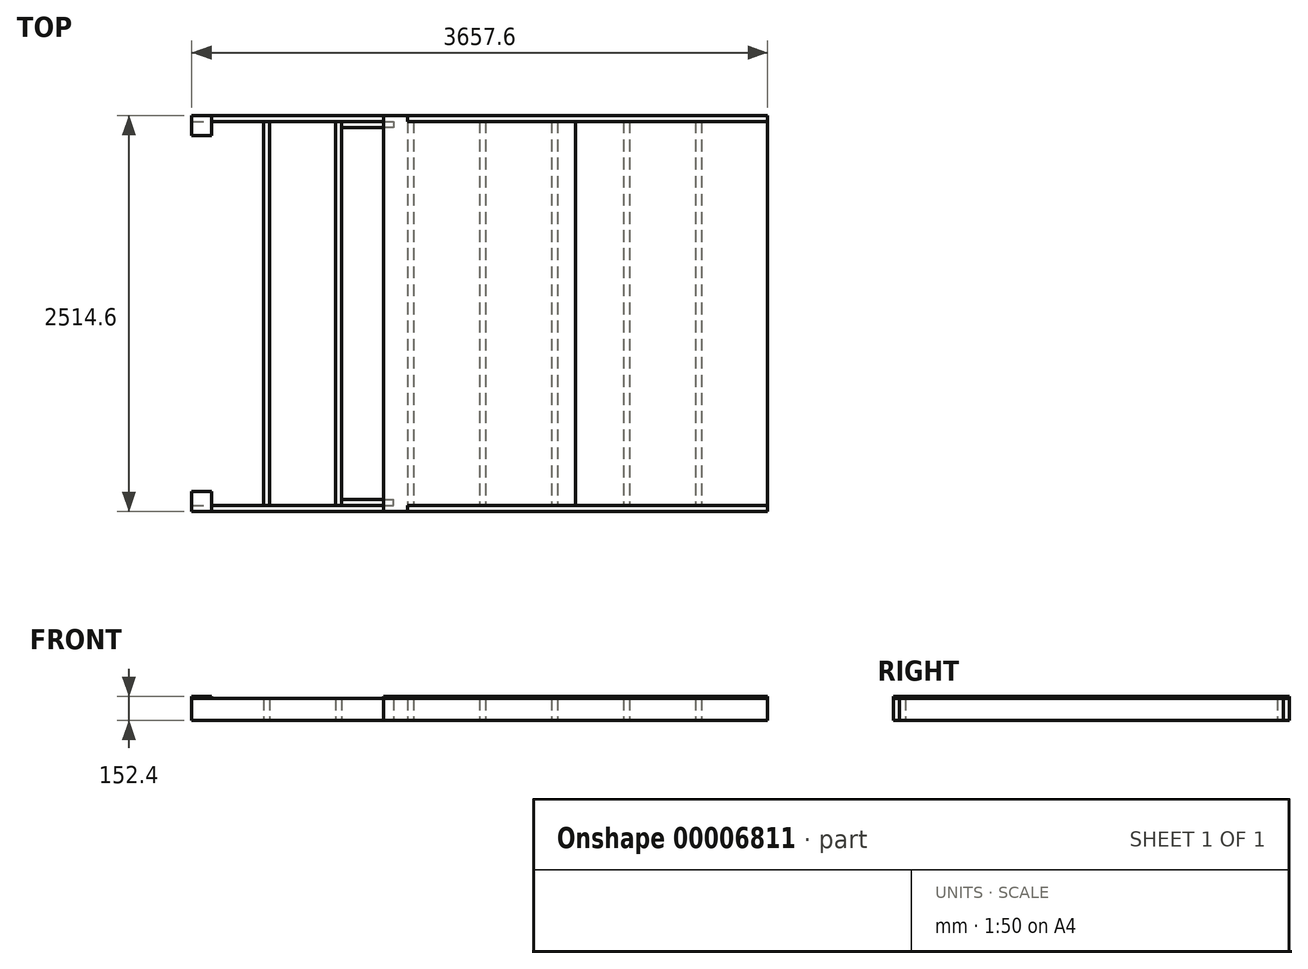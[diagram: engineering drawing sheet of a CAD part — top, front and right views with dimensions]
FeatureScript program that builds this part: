
annotation { "Feature Type Name" : "Feature", "Feature Type Description" : "" }
export const myFeature = defineFeature(function(context is Context, id is Id, definition is map)
    precondition{}
    {
        {
            var Q0;
            Q0=qCreatedBy(makeId("Top.planeOp"),FACE);
            var sketch = newSketch(context, id + "F0", { "sketchPlane" : qUnion([Q0])});
            skLineSegment(sketch, "E0.rect.bottom", {"start": v(1828.8, 1257.3) * mm, "end": v(-1828.8, 1257.3) * mm, "construction": true});
            skLineSegment(sketch, "E0.rect.top", {"start": v(1828.8, -1257.3) * mm, "end": v(-1828.8, -1257.3) * mm, "construction": true});
            skLineSegment(sketch, "E0.rect.left", {"start": v(1828.8, 1257.3) * mm, "end": v(1828.8, -1257.3) * mm, "construction": true});
            skLineSegment(sketch, "E0.rect.right", {"start": v(-1828.8, 1257.3) * mm, "end": v(-1828.8, -1257.3) * mm, "construction": true});
            skPoint(sketch, "E0.rect.middle", {"position": v(0, 0) * mm});
            skLineSegment(sketch, "E1.bottom", {"start": v(-1828.8, 1257.3) * mm, "end": v(-609.6, 1257.3) * mm});
            skLineSegment(sketch, "E1.top", {"start": v(-1828.8, 1219.2) * mm, "end": v(-609.6, 1219.2) * mm});
            skLineSegment(sketch, "E1.left", {"start": v(-1828.8, 1257.3) * mm, "end": v(-1828.8, 1219.2) * mm});
            skLineSegment(sketch, "E1.right", {"start": v(-609.6, 1257.3) * mm, "end": v(-609.6, 1219.2) * mm});
            skLineSegment(sketch, "E2.bottom", {"start": v(-1828.8, -1257.3) * mm, "end": v(-609.6, -1257.3) * mm});
            skLineSegment(sketch, "E2.top", {"start": v(-1828.8, -1219.2) * mm, "end": v(-609.6, -1219.2) * mm});
            skLineSegment(sketch, "E2.left", {"start": v(-1828.8, -1257.3) * mm, "end": v(-1828.8, -1219.2) * mm});
            skLineSegment(sketch, "E2.right", {"start": v(-609.6, -1257.3) * mm, "end": v(-609.6, -1219.2) * mm});
            skLineSegment(sketch, "E3.bottom", {"start": v(-1828.8, 1219.2) * mm, "end": v(-1790.7, 1219.2) * mm});
            skLineSegment(sketch, "E3.top", {"start": v(-1828.8, -1219.2) * mm, "end": v(-1790.7, -1219.2) * mm});
            skLineSegment(sketch, "E3.left", {"start": v(-1828.8, 1219.2) * mm, "end": v(-1828.8, -1219.2) * mm});
            skLineSegment(sketch, "E3.right", {"start": v(-1790.7, 1219.2) * mm, "end": v(-1790.7, -1219.2) * mm});
            skLineSegment(sketch, "E4.1.0.0", {"start": v(-1371.6, 1219.2) * mm, "end": v(-1371.6, -1219.2) * mm});
            skLineSegment(sketch, "E4.1.0.1", {"start": v(-1333.5, 1219.2) * mm, "end": v(-1333.5, -1219.2) * mm});
            skLineSegment(sketch, "E4.2.0.0", {"start": v(-914.4, 1219.2) * mm, "end": v(-914.4, -1219.2) * mm});
            skLineSegment(sketch, "E4.2.0.1", {"start": v(-876.3, 1219.2) * mm, "end": v(-876.3, -1219.2) * mm});
            skLineSegment(sketch, "E4.3.0.0", {"start": v(-457.2, 1219.2) * mm, "end": v(-457.2, -1219.2) * mm});
            skLineSegment(sketch, "E4.3.0.1", {"start": v(-419.1, 1219.2) * mm, "end": v(-419.1, -1219.2) * mm});
            skLineSegment(sketch, "E4.4.0.0", {"start": v(0, 1219.2) * mm, "end": v(0, -1219.2) * mm});
            skLineSegment(sketch, "E4.4.0.1", {"start": v(38.1, 1219.2) * mm, "end": v(38.1, -1219.2) * mm});
            skLineSegment(sketch, "E4.5.0.0", {"start": v(457.2, 1219.2) * mm, "end": v(457.2, -1219.2) * mm});
            skLineSegment(sketch, "E4.5.0.1", {"start": v(495.3, 1219.2) * mm, "end": v(495.3, -1219.2) * mm});
            skLineSegment(sketch, "E4.6.0.0", {"start": v(914.4, 1219.2) * mm, "end": v(914.4, -1219.2) * mm});
            skLineSegment(sketch, "E4.6.0.1", {"start": v(952.5, 1219.2) * mm, "end": v(952.5, -1219.2) * mm});
            skLineSegment(sketch, "E4.7.0.0", {"start": v(1371.6, 1219.2) * mm, "end": v(1371.6, -1219.2) * mm});
            skLineSegment(sketch, "E4.7.0.1", {"start": v(1409.7, 1219.2) * mm, "end": v(1409.7, -1219.2) * mm});
            skLineSegment(sketch, "E4.direction1", {"start": v(-1828.8, -1219.2) * mm, "end": v(-1371.6, -1219.2) * mm, "construction": true});
            skLineSegment(sketch, "E5.bottom", {"start": v(-609.6, -1219.2) * mm, "end": v(1828.8, -1219.2) * mm});
            skLineSegment(sketch, "E5.top", {"start": v(-609.6, -1257.3) * mm, "end": v(1828.8, -1257.3) * mm});
            skLineSegment(sketch, "E5.left", {"start": v(-609.6, -1219.2) * mm, "end": v(-609.6, -1257.3) * mm});
            skLineSegment(sketch, "E5.right", {"start": v(1828.8, -1219.2) * mm, "end": v(1828.8, -1257.3) * mm});
            skLineSegment(sketch, "E6.bottom", {"start": v(-609.6, 1219.2) * mm, "end": v(1828.8, 1219.2) * mm});
            skLineSegment(sketch, "E6.top", {"start": v(-609.6, 1257.3) * mm, "end": v(1828.8, 1257.3) * mm});
            skLineSegment(sketch, "E6.left", {"start": v(-609.6, 1219.2) * mm, "end": v(-609.6, 1257.3) * mm});
            skLineSegment(sketch, "E6.right", {"start": v(1828.8, 1219.2) * mm, "end": v(1828.8, 1257.3) * mm});
            skLineSegment(sketch, "E7.bottom", {"start": v(-546.1, 1219.2) * mm, "end": v(-876.3, 1219.2) * mm});
            skLineSegment(sketch, "E7.top", {"start": v(-546.1, 1181.1) * mm, "end": v(-876.3, 1181.1) * mm});
            skLineSegment(sketch, "E7.left", {"start": v(-546.1, 1219.2) * mm, "end": v(-546.1, 1181.1) * mm});
            skLineSegment(sketch, "E7.right", {"start": v(-876.3, 1219.2) * mm, "end": v(-876.3, 1181.1) * mm});
            skLineSegment(sketch, "E8.bottom", {"start": v(-876.3, -1219.2) * mm, "end": v(-546.1, -1219.2) * mm});
            skLineSegment(sketch, "E8.top", {"start": v(-876.3, -1181.1) * mm, "end": v(-546.1, -1181.1) * mm});
            skLineSegment(sketch, "E8.left", {"start": v(-876.3, -1219.2) * mm, "end": v(-876.3, -1181.1) * mm});
            skLineSegment(sketch, "E8.right", {"start": v(-546.1, -1219.2) * mm, "end": v(-546.1, -1181.1) * mm});
            skSolve(sketch);
        }
        {
            var Q0;
            Q0=makeQuery(id+"F0.imprint","IMPRINT",FACE,{"disambiguationData":[TD([[makeQuery(id+"F0.imprint","IMPRINT",EDGE,{"derivedFrom":sQuery(id+"F0.wireOp",EDGE,"E1.bottom")}),-1.0]])]});
            var Q1;
            Q1=makeQuery(id+"F0.imprint","IMPRINT",FACE,{"disambiguationData":[TD([[makeQuery(id+"F0.imprint","IMPRINT",EDGE,{"derivedFrom":sQuery(id+"F0.wireOp",EDGE,"E2.bottom")}),1.0]])]});
            extrude(context, id + "F1", {"entities" : qUnion([Q0, Q1]), "depth" : 139.7 * mm});
        }
        {
            var Q0;
            Q0=makeQuery(id+"F0.imprint","IMPRINT",FACE,{"disambiguationData":[TD([[makeQuery(id+"F0.imprint","IMPRINT",EDGE,{"derivedFrom":sQuery(id+"F0.wireOp",EDGE,"E3.bottom")}),-1.0]])]});
            var Q1;
            {var subQ1=sQuery(id+"F0.wireOp",EDGE,"E4.1.0.0");Q1=makeQuery(id+"F0.imprint","IMPRINT",FACE,{"disambiguationData":[TD([[makeQuery(id+"F0.imprint","IMPRINT",EDGE,{"derivedFrom":subQ1}),1.0]])]});}
            var Q2;
            {var subQ1=sQuery(id+"F0.wireOp",EDGE,"E4.2.0.0");Q2=makeQuery(id+"F0.imprint","IMPRINT",FACE,{"disambiguationData":[TD([[makeQuery(id+"F0.imprint","IMPRINT",EDGE,{"derivedFrom":subQ1}),1.0]])]});}
            var Q3;
            {var subQ1=sQuery(id+"F0.wireOp",EDGE,"E4.3.0.0");Q3=makeQuery(id+"F0.imprint","IMPRINT",FACE,{"disambiguationData":[TD([[makeQuery(id+"F0.imprint","IMPRINT",EDGE,{"derivedFrom":subQ1}),1.0]])]});}
            var Q4;
            {var subQ1=sQuery(id+"F0.wireOp",EDGE,"E4.4.0.0");Q4=makeQuery(id+"F0.imprint","IMPRINT",FACE,{"disambiguationData":[TD([[makeQuery(id+"F0.imprint","IMPRINT",EDGE,{"derivedFrom":subQ1}),1.0]])]});}
            var Q5;
            {var subQ1=sQuery(id+"F0.wireOp",EDGE,"E4.5.0.0");Q5=makeQuery(id+"F0.imprint","IMPRINT",FACE,{"disambiguationData":[TD([[makeQuery(id+"F0.imprint","IMPRINT",EDGE,{"derivedFrom":subQ1}),1.0]])]});}
            var Q6;
            {var subQ1=sQuery(id+"F0.wireOp",EDGE,"E4.6.0.0");Q6=makeQuery(id+"F0.imprint","IMPRINT",FACE,{"disambiguationData":[TD([[makeQuery(id+"F0.imprint","IMPRINT",EDGE,{"derivedFrom":subQ1}),1.0]])]});}
            var Q7;
            {var subQ1=sQuery(id+"F0.wireOp",EDGE,"E4.7.0.0");Q7=makeQuery(id+"F0.imprint","IMPRINT",FACE,{"disambiguationData":[TD([[makeQuery(id+"F0.imprint","IMPRINT",EDGE,{"derivedFrom":subQ1}),1.0]])]});}
            extrude(context, id + "F2", {"entities" : qUnion([Q0, Q1, Q2, Q3, Q4, Q5, Q6, Q7]), "depth" : 139.7 * mm});
        }
        {
            var Q0;
            Q0=makeQuery(id+"F0.imprint","IMPRINT",FACE,{"disambiguationData":[TD([[makeQuery(id+"F0.imprint","IMPRINT",EDGE,{"derivedFrom":sQuery(id+"F0.wireOp",EDGE,"E6.top")}),-1.0]])]});
            var Q1;
            Q1=makeQuery(id+"F0.imprint","IMPRINT",FACE,{"disambiguationData":[TD([[makeQuery(id+"F0.imprint","IMPRINT",EDGE,{"derivedFrom":sQuery(id+"F0.wireOp",EDGE,"E5.top")}),1.0]])]});
            extrude(context, id + "F3", {"entities" : qUnion([Q0, Q1]), "depth" : 139.7 * mm});
        }
        {
            var Q0;
            Q0=makeQuery(id+"F0.imprint","IMPRINT",FACE,{"disambiguationData":[TD([[makeQuery(id+"F0.imprint","IMPRINT",EDGE,{"derivedFrom":sQuery(id+"F0.wireOp",EDGE,"E8.top")}),-1.0]])]});
            var Q1;
            Q1=makeQuery(id+"F0.imprint","IMPRINT",FACE,{"disambiguationData":[TD([[makeQuery(id+"F0.imprint","IMPRINT",EDGE,{"derivedFrom":sQuery(id+"F0.wireOp",EDGE,"E7.top")}),-1.0]])]});
            extrude(context, id + "F4", {"entities" : qUnion([Q0, Q1]), "depth" : 139.7 * mm});
        }
        {
            var Q0;
            Q0=makeQuery(id+"F1.opExtrude","CAP_FACE",FACE,{"disambiguationData":[OSD([sQuery(id+"F0.wireOp",EDGE,"E1.bottom"),sQuery(id+"F0.wireOp",EDGE,"E1.top"),sQuery(id+"F0.wireOp",EDGE,"E1.left"),sQuery(id+"F0.wireOp",EDGE,"E3.bottom"),sQuery(id+"F0.wireOp",EDGE,"E6.left"),sQuery(id+"F0.wireOp",EDGE,"E7.bottom")])],"isStart":false});
            var sketch = newSketch(context, id + "F5", { "sketchPlane" : qUnion([Q0])});
            skLineSegment(sketch, "E9.bottom", {"start": v(-1828.8, 1257.3) * mm, "end": v(-609.6, 1257.3) * mm});
            skLineSegment(sketch, "E9.top", {"start": v(-1828.8, -1257.3) * mm, "end": v(-609.6, -1257.3) * mm});
            skLineSegment(sketch, "E9.left", {"start": v(-1828.8, 1257.3) * mm, "end": v(-1828.8, -1257.3) * mm});
            skLineSegment(sketch, "E9.right", {"start": v(-609.6, 1257.3) * mm, "end": v(-609.6, -1257.3) * mm});
            skLineSegment(sketch, "E10.bottom", {"start": v(-609.6, 1257.3) * mm, "end": v(609.6, 1257.3) * mm});
            skLineSegment(sketch, "E10.top", {"start": v(-609.6, -1257.3) * mm, "end": v(609.6, -1257.3) * mm});
            skLineSegment(sketch, "E10.right", {"start": v(609.6, 1257.3) * mm, "end": v(609.6, -1257.3) * mm});
            skLineSegment(sketch, "E11.bottom", {"start": v(609.6, 1257.3) * mm, "end": v(1828.8, 1257.3) * mm});
            skLineSegment(sketch, "E11.top", {"start": v(609.6, -1257.3) * mm, "end": v(1828.8, -1257.3) * mm});
            skLineSegment(sketch, "E11.right", {"start": v(1828.8, 1257.3) * mm, "end": v(1828.8, -1257.3) * mm});
            skLineSegment(sketch, "E12.bottom", {"start": v(-1828.8, -1257.3) * mm, "end": v(-1701.8, -1257.3) * mm});
            skLineSegment(sketch, "E12.top", {"start": v(-1828.8, -1130.3) * mm, "end": v(-1701.8, -1130.3) * mm});
            skLineSegment(sketch, "E12.left", {"start": v(-1828.8, -1257.3) * mm, "end": v(-1828.8, -1130.3) * mm});
            skLineSegment(sketch, "E12.right", {"start": v(-1701.8, -1257.3) * mm, "end": v(-1701.8, -1130.3) * mm});
            skLineSegment(sketch, "E13.bottom", {"start": v(-1828.8, 1257.3) * mm, "end": v(-1701.8, 1257.3) * mm});
            skLineSegment(sketch, "E13.top", {"start": v(-1828.8, 1130.3) * mm, "end": v(-1701.8, 1130.3) * mm});
            skLineSegment(sketch, "E13.left", {"start": v(-1828.8, 1257.3) * mm, "end": v(-1828.8, 1130.3) * mm});
            skLineSegment(sketch, "E13.right", {"start": v(-1701.8, 1257.3) * mm, "end": v(-1701.8, 1130.3) * mm});
            skLineSegment(sketch, "E14.bottom", {"start": v(-609.6, -1257.3) * mm, "end": v(-457.2, -1257.3) * mm});
            skLineSegment(sketch, "E14.top", {"start": v(-609.6, -1130.3) * mm, "end": v(-457.2, -1130.3) * mm});
            skLineSegment(sketch, "E14.left", {"start": v(-609.6, -1257.3) * mm, "end": v(-609.6, -1130.3) * mm});
            skLineSegment(sketch, "E14.right", {"start": v(-457.2, -1257.3) * mm, "end": v(-457.2, -1130.3) * mm});
            skLineSegment(sketch, "E15.bottom", {"start": v(-609.6, 1257.3) * mm, "end": v(-457.2, 1257.3) * mm});
            skLineSegment(sketch, "E15.top", {"start": v(-609.6, 1130.3) * mm, "end": v(-457.2, 1130.3) * mm});
            skLineSegment(sketch, "E15.left", {"start": v(-609.6, 1257.3) * mm, "end": v(-609.6, 1130.3) * mm});
            skLineSegment(sketch, "E15.right", {"start": v(-457.2, 1257.3) * mm, "end": v(-457.2, 1130.3) * mm});
            skLineSegment(sketch, "E16.0", {"start": v(-457.2, 1219.2) * mm, "end": v(-457.2, -1219.2) * mm});
            skLineSegment(sketch, "E17.0", {"start": v(-1828.8, -1219.2) * mm, "end": v(-609.6, -1219.2) * mm});
            skLineSegment(sketch, "E18.0", {"start": v(-609.6, -1219.2) * mm, "end": v(1828.8, -1219.2) * mm});
            skLineSegment(sketch, "E19.0", {"start": v(1828.8, 1219.2) * mm, "end": v(-609.6, 1219.2) * mm});
            skSolve(sketch);
        }
        {
            var Q0;
            Q0=makeQuery(id+"F5.imprint","IMPRINT",FACE,{"disambiguationData":[TD([[makeQuery(id+"F5.imprint","IMPRINT",EDGE,{"derivedFrom":sQuery(id+"F5.wireOp",EDGE,"E9.left")}),1.0]])]});
            var Q1;
            {var subQ0=sQuery(id+"F5.wireOp",EDGE,"E19.0");var subQ1=sQuery(id+"F5.wireOp",EDGE,"E10.right");var subQ2=makeQuery(id+"F5.imprint","INTERSECT",VERTEX,{"derivedFrom":[subQ1,subQ0]});Q1=makeQuery(id+"F5.imprint","IMPRINT",FACE,{"disambiguationData":[TD([[makeQuery(id+"F5.imprint","IMPRINT",EDGE,{"disambiguationData":[TD([[subQ2,-1.0]])],"derivedFrom":subQ1}),1.0]])]});}
            extrude(context, id + "F6", {"entities" : qUnion([Q0, Q1]), "depth" : 12.7 * mm});
        }
        {
            var Q0;
            {var subQ0=sQuery(id+"F5.wireOp",EDGE,"E19.0");var subQ1=sQuery(id+"F5.wireOp",EDGE,"E10.right");var subQ2=makeQuery(id+"F5.imprint","INTERSECT",VERTEX,{"derivedFrom":[subQ1,subQ0]});Q0=makeQuery(id+"F5.imprint","IMPRINT",FACE,{"disambiguationData":[TD([[makeQuery(id+"F5.imprint","IMPRINT",EDGE,{"disambiguationData":[TD([[subQ2,-1.0]])],"derivedFrom":subQ1}),-1.0]])]});}
            var Q1;
            Q1=makeQuery(id+"F5.imprint","IMPRINT",FACE,{"disambiguationData":[TD([[makeQuery(id+"F5.imprint","IMPRINT",EDGE,{"derivedFrom":sQuery(id+"F5.wireOp",EDGE,"E9.right")}),1.0]])]});
            extrude(context, id + "F7", {"entities" : qUnion([Q0, Q1]), "depth" : 12.7 * mm});
        }
    });
